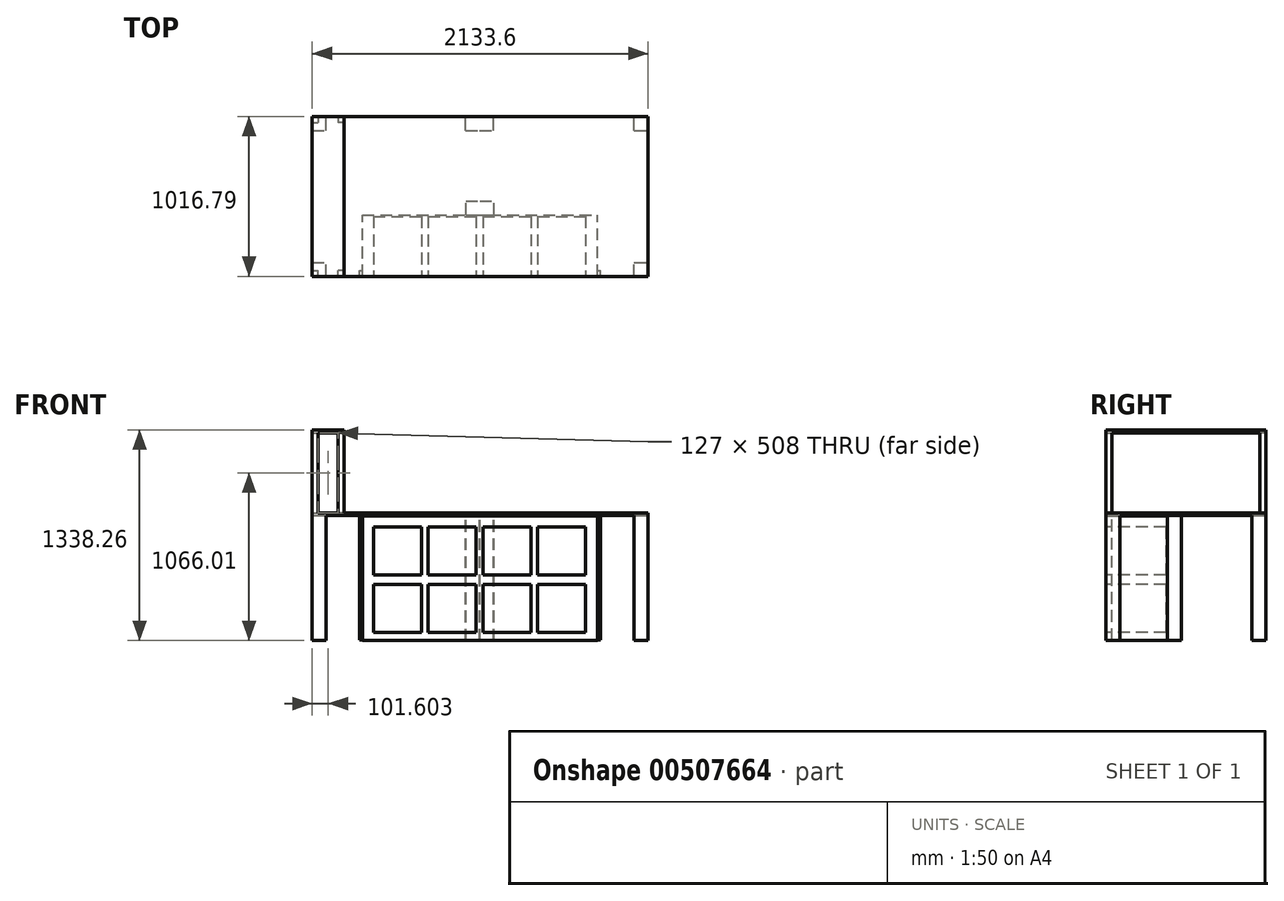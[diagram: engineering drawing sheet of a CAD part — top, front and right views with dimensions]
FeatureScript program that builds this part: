
annotation { "Feature Type Name" : "Feature", "Feature Type Description" : "" }
export const myFeature = defineFeature(function(context is Context, id is Id, definition is map)
    precondition{}
    {
        {
            var Q0;
            Q0=qCreatedBy(makeId("Top.planeOp"),FACE);
            var sketch = newSketch(context, id + "F0", { "sketchPlane" : qUnion([Q0])});
            skLineSegment(sketch, "E0", {"start": v(-1062.93, -24.93) * mm, "end": v(1070.67, -24.93) * mm});
            skLineSegment(sketch, "E1", {"start": v(-1062.93, -24.93) * mm, "end": v(-1062.93, -1040.93) * mm});
            skLineSegment(sketch, "E2", {"start": v(-1062.93, -1040.93) * mm, "end": v(1070.67, -1040.93) * mm});
            skLineSegment(sketch, "E3", {"start": v(1070.67, -1040.93) * mm, "end": v(1070.67, -24.93) * mm});
            skLineSegment(sketch, "E4", {"start": v(0, -1040.93) * mm, "end": v(0, -24.93) * mm});
            skSolve(sketch);
        }
        {
            var Q0;
            {var subQ0=sQuery(id+"F0.wireOp",EDGE,"E1");Q0=makeQuery(id+"F0.imprint","IMPRINT",FACE,{"disambiguationData":[TD([[makeQuery(id+"F0.imprint","IMPRINT",EDGE,{"derivedFrom":subQ0}),1.0]])]});}
            var Q1;
            {var subQ0=sQuery(id+"F0.wireOp",EDGE,"E3");Q1=makeQuery(id+"F0.imprint","IMPRINT",FACE,{"disambiguationData":[TD([[makeQuery(id+"F0.imprint","IMPRINT",EDGE,{"derivedFrom":subQ0}),1.0]])]});}
            extrude(context, id + "F1", {"entities" : qUnion([Q0, Q1]), "depth" : 18.26 * mm});
        }
        {
            var Q0;
            Q0=makeQuery(id+"F1.opExtrude","CAP_FACE",FACE,{"disambiguationData":[OSD([sQuery(id+"F0.wireOp",EDGE,"E0"),sQuery(id+"F0.wireOp",EDGE,"E1"),sQuery(id+"F0.wireOp",EDGE,"E2"),sQuery(id+"F0.wireOp",EDGE,"E3")])],"isStart":true});
            var sketch = newSketch(context, id + "F2", { "sketchPlane" : qUnion([Q0])});
            skLineSegment(sketch, "E5", {"start": v(3.87, 1040.93) * mm, "end": v(0, 24.93) * mm, "construction": true});
            skPoint(sketch, "E5.endSnap0", {"position": v(3.87, 24.93) * mm});
            skLineSegment(sketch, "E6.bottom", {"start": v(-743.74, 1040.93) * mm, "end": v(748.5, 1040.93) * mm});
            skLineSegment(sketch, "E6.top", {"start": v(-743.74, 650.4) * mm, "end": v(748.5, 650.4) * mm, "construction": true});
            skLineSegment(sketch, "E6.left", {"start": v(-743.74, 1040.93) * mm, "end": v(-743.74, 650.4) * mm, "construction": true});
            skLineSegment(sketch, "E6.right", {"start": v(748.5, 1040.93) * mm, "end": v(748.5, 650.4) * mm, "construction": true});
            skLineSegment(sketch, "E7", {"start": v(2.38, 650.4) * mm, "end": v(2.38, 1040.93) * mm, "construction": true});
            skLineSegment(sketch, "E8.bottom", {"start": v(-1062.93, 1040.93) * mm, "end": v(-974.03, 1040.93) * mm});
            skLineSegment(sketch, "E8.top", {"start": v(-1062.93, 952.03) * mm, "end": v(-974.03, 952.03) * mm});
            skLineSegment(sketch, "E8.left", {"start": v(-1062.93, 1040.93) * mm, "end": v(-1062.93, 952.03) * mm});
            skLineSegment(sketch, "E8.right", {"start": v(-974.03, 1040.93) * mm, "end": v(-974.03, 952.03) * mm});
            skLineSegment(sketch, "E9.bottom", {"start": v(-1062.93, 113.83) * mm, "end": v(-974.03, 113.83) * mm});
            skLineSegment(sketch, "E9.top", {"start": v(-1062.93, 24.93) * mm, "end": v(-974.03, 24.93) * mm});
            skLineSegment(sketch, "E9.left", {"start": v(-1062.93, 113.83) * mm, "end": v(-1062.93, 24.93) * mm});
            skLineSegment(sketch, "E9.right", {"start": v(-974.03, 113.83) * mm, "end": v(-974.03, 24.93) * mm});
            skLineSegment(sketch, "E10.bottom", {"start": v(981.77, 113.83) * mm, "end": v(1070.67, 113.83) * mm});
            skLineSegment(sketch, "E10.top", {"start": v(981.77, 24.93) * mm, "end": v(1070.67, 24.93) * mm});
            skLineSegment(sketch, "E10.left", {"start": v(981.77, 113.83) * mm, "end": v(981.77, 24.93) * mm});
            skLineSegment(sketch, "E10.right", {"start": v(1070.67, 113.83) * mm, "end": v(1070.67, 24.93) * mm});
            skLineSegment(sketch, "E11.bottom", {"start": v(981.77, 1040.93) * mm, "end": v(1070.67, 1040.93) * mm});
            skLineSegment(sketch, "E11.top", {"start": v(981.77, 952.03) * mm, "end": v(1070.67, 952.03) * mm});
            skLineSegment(sketch, "E11.left", {"start": v(981.77, 1040.93) * mm, "end": v(981.77, 952.03) * mm});
            skLineSegment(sketch, "E11.right", {"start": v(1070.67, 1040.93) * mm, "end": v(1070.67, 952.03) * mm});
            skLineSegment(sketch, "E12.bottom", {"start": v(-86.52, 650.4) * mm, "end": v(2.38, 650.4) * mm});
            skLineSegment(sketch, "E12.top", {"start": v(-86.86, 561.5) * mm, "end": v(2.05, 561.5) * mm});
            skLineSegment(sketch, "E12.left", {"start": v(-86.52, 650.4) * mm, "end": v(-86.86, 561.5) * mm});
            skLineSegment(sketch, "E12.right", {"start": v(2.38, 650.4) * mm, "end": v(2.05, 561.5) * mm});
            skLineSegment(sketch, "E13.bottom", {"start": v(-88.56, 113.83) * mm, "end": v(0.34, 113.83) * mm});
            skLineSegment(sketch, "E13.top", {"start": v(-88.9, 24.93) * mm, "end": v(0, 24.93) * mm});
            skLineSegment(sketch, "E13.left", {"start": v(-88.56, 113.83) * mm, "end": v(-88.9, 24.93) * mm});
            skLineSegment(sketch, "E13.right", {"start": v(0.34, 113.83) * mm, "end": v(0, 24.93) * mm});
            skLineSegment(sketch, "E14.bottom", {"start": v(2.38, 650.4) * mm, "end": v(91.28, 650.07) * mm});
            skLineSegment(sketch, "E14.top", {"start": v(2.05, 561.5) * mm, "end": v(90.94, 561.17) * mm});
            skLineSegment(sketch, "E14.right", {"start": v(91.28, 650.07) * mm, "end": v(90.94, 561.17) * mm});
            skLineSegment(sketch, "E15.bottom", {"start": v(0.34, 113.83) * mm, "end": v(89.24, 113.5) * mm});
            skLineSegment(sketch, "E15.top", {"start": v(0, 24.93) * mm, "end": v(88.9, 24.6) * mm});
            skLineSegment(sketch, "E15.right", {"start": v(89.24, 113.5) * mm, "end": v(88.9, 24.6) * mm});
            skSolve(sketch);
        }
        {
            var Q0;
            Q0 = qSketchRegion(id + "F2", true);
            extrude(context, id + "F3", {"entities" : qUnion([Q0]), "operationType" : NewBodyOperationType.ADD, "depth" : 793.75 * mm});
        }
        {
            var Q0;
            {var subQ6=sQuery(id+"F2.wireOp",EDGE,"E6.bottom");Q0=makeQuery(id+"F2.imprint","IMPRINT",FACE,{"disambiguationData":[TD([[makeQuery(id+"F2.imprint","IMPRINT",EDGE,{"derivedFrom":subQ6}),-1.0]])]});}
            cPlane(context, id + "F4", {"entities" : qUnion([Q0]), "cplaneType" : CPlaneType.OFFSET, "offset" : 3.17 * mm, "width" : 152.4 * mm, "height" : 152.4 * mm});
        }
        {
            var Q0;
            Q0=qCreatedBy(id+"F4.planeOp",FACE);
            var sketch = newSketch(context, id + "F5", { "sketchPlane" : qUnion([Q0])});
            skLineSegment(sketch, "E16", {"start": v(-744, 1041.4) * mm, "end": v(-744, 651.87) * mm});
            skLineSegment(sketch, "E17", {"start": v(-744, 651.87) * mm, "end": v(748.46, 651.87) * mm});
            skLineSegment(sketch, "E18", {"start": v(748.5, 1041.2) * mm, "end": v(748.46, 651.87) * mm});
            skLineSegment(sketch, "E19", {"start": v(-744, 1041.4) * mm, "end": v(748.5, 1041.2) * mm});
            skSolve(sketch);
        }
        {
            var Q0;
            Q0=makeQuery(id+"F5.imprint","IMPRINT",FACE,{"disambiguationData":[TD([[makeQuery(id+"F5.imprint","IMPRINT",EDGE,{"derivedFrom":sQuery(id+"F5.wireOp",EDGE,"E16")}),1.0]])]});
            extrude(context, id + "F6", {"entities" : qUnion([Q0]), "depth" : 790.57 * mm});
        }
        {
            var Q0;
            Q0=makeQuery(id+"F6.opExtrude","SWEPT_FACE",FACE,{"disambiguationData":[OSD([sQuery(id+"F5.wireOp",EDGE,"E19")])]});
            var sketch = newSketch(context, id + "F7", { "sketchPlane" : qUnion([Q0])});
            skLineSegment(sketch, "E20.bottom", {"start": v(-674.52, -72.87) * mm, "end": v(-369.72, -72.87) * mm});
            skLineSegment(sketch, "E20.top", {"start": v(-674.52, -377.67) * mm, "end": v(-369.72, -377.67) * mm});
            skLineSegment(sketch, "E20.left", {"start": v(-674.52, -72.87) * mm, "end": v(-674.52, -377.67) * mm});
            skLineSegment(sketch, "E20.right", {"start": v(-369.72, -72.87) * mm, "end": v(-369.72, -377.67) * mm});
            skLineSegment(sketch, "E21.0.1.0", {"start": v(-369.72, -436.09) * mm, "end": v(-369.72, -740.89) * mm});
            skLineSegment(sketch, "E21.0.1.1", {"start": v(-674.52, -436.09) * mm, "end": v(-674.52, -740.89) * mm});
            skLineSegment(sketch, "E21.0.1.2", {"start": v(-674.52, -740.89) * mm, "end": v(-369.72, -740.89) * mm});
            skLineSegment(sketch, "E21.0.1.3", {"start": v(-674.52, -436.09) * mm, "end": v(-369.72, -436.09) * mm});
            skLineSegment(sketch, "E21.1.0.0", {"start": v(-21.74, -72.87) * mm, "end": v(-21.74, -377.67) * mm});
            skLineSegment(sketch, "E21.1.0.1", {"start": v(-326.54, -72.87) * mm, "end": v(-326.54, -377.67) * mm});
            skLineSegment(sketch, "E21.1.0.2", {"start": v(-326.54, -377.67) * mm, "end": v(-21.74, -377.67) * mm});
            skLineSegment(sketch, "E21.1.0.3", {"start": v(-326.54, -72.87) * mm, "end": v(-21.74, -72.87) * mm});
            skLineSegment(sketch, "E21.1.1.0", {"start": v(-21.74, -436.09) * mm, "end": v(-21.74, -740.89) * mm});
            skLineSegment(sketch, "E21.1.1.1", {"start": v(-326.54, -436.09) * mm, "end": v(-326.54, -740.89) * mm});
            skLineSegment(sketch, "E21.1.1.2", {"start": v(-326.54, -740.89) * mm, "end": v(-21.74, -740.89) * mm});
            skLineSegment(sketch, "E21.1.1.3", {"start": v(-326.54, -436.09) * mm, "end": v(-21.74, -436.09) * mm});
            skLineSegment(sketch, "E21.2.0.0", {"start": v(326.24, -72.87) * mm, "end": v(326.24, -377.67) * mm});
            skLineSegment(sketch, "E21.2.0.1", {"start": v(21.44, -72.87) * mm, "end": v(21.44, -377.67) * mm});
            skLineSegment(sketch, "E21.2.0.2", {"start": v(21.44, -377.67) * mm, "end": v(326.24, -377.67) * mm});
            skLineSegment(sketch, "E21.2.0.3", {"start": v(21.44, -72.87) * mm, "end": v(326.24, -72.87) * mm});
            skLineSegment(sketch, "E21.2.1.0", {"start": v(326.24, -436.09) * mm, "end": v(326.24, -740.89) * mm});
            skLineSegment(sketch, "E21.2.1.1", {"start": v(21.44, -436.09) * mm, "end": v(21.44, -740.89) * mm});
            skLineSegment(sketch, "E21.2.1.2", {"start": v(21.44, -740.89) * mm, "end": v(326.24, -740.89) * mm});
            skLineSegment(sketch, "E21.2.1.3", {"start": v(21.44, -436.09) * mm, "end": v(326.24, -436.09) * mm});
            skLineSegment(sketch, "E21.3.0.0", {"start": v(674.22, -72.87) * mm, "end": v(674.22, -377.67) * mm});
            skLineSegment(sketch, "E21.3.0.1", {"start": v(369.42, -72.87) * mm, "end": v(369.42, -377.67) * mm});
            skLineSegment(sketch, "E21.3.0.2", {"start": v(369.42, -377.67) * mm, "end": v(674.22, -377.67) * mm});
            skLineSegment(sketch, "E21.3.0.3", {"start": v(369.42, -72.87) * mm, "end": v(674.22, -72.87) * mm});
            skLineSegment(sketch, "E21.3.1.0", {"start": v(674.22, -436.09) * mm, "end": v(674.22, -740.89) * mm});
            skLineSegment(sketch, "E21.3.1.1", {"start": v(369.42, -436.09) * mm, "end": v(369.42, -740.89) * mm});
            skLineSegment(sketch, "E21.3.1.2", {"start": v(369.42, -740.89) * mm, "end": v(674.22, -740.89) * mm});
            skLineSegment(sketch, "E21.3.1.3", {"start": v(369.42, -436.09) * mm, "end": v(674.22, -436.09) * mm});
            skLineSegment(sketch, "E21.direction1", {"start": v(-674.52, -377.67) * mm, "end": v(-326.54, -377.67) * mm, "construction": true});
            skLineSegment(sketch, "E21.direction2", {"start": v(-674.52, -377.67) * mm, "end": v(-674.52, -740.89) * mm, "construction": true});
            skSolve(sketch);
        }
        {
            var Q0;
            Q0 = qSketchRegion(id + "F7", true);
            extrude(context, id + "F8", {"entities" : qUnion([Q0]), "operationType" : NewBodyOperationType.REMOVE, "oppositeDirection" : true, "depth" : 381 * mm});
        }
        {
            var Q0;
            {var subQ6=sQuery(id+"F2.wireOp",EDGE,"E6.bottom");Q0=makeQuery(id+"F2.imprint","IMPRINT",FACE,{"disambiguationData":[TD([[makeQuery(id+"F2.imprint","IMPRINT",EDGE,{"derivedFrom":subQ6}),-1.0]])]});}
            var sketch = newSketch(context, id + "F9", { "sketchPlane" : qUnion([Q0])});
            skLineSegment(sketch, "E22.bottom", {"start": v(748.8, 1040.9) * mm, "end": v(767.86, 1040.9) * mm});
            skLineSegment(sketch, "E22.top", {"start": v(748.8, 1002.8) * mm, "end": v(767.86, 1002.8) * mm});
            skLineSegment(sketch, "E22.left", {"start": v(748.8, 1040.9) * mm, "end": v(748.8, 1002.8) * mm});
            skLineSegment(sketch, "E22.right", {"start": v(767.86, 1040.9) * mm, "end": v(767.86, 1002.8) * mm});
            skLineSegment(sketch, "E23.bottom", {"start": v(-763.16, 1040.9) * mm, "end": v(-744.11, 1040.9) * mm});
            skLineSegment(sketch, "E23.top", {"start": v(-763.16, 1002.8) * mm, "end": v(-744.11, 1002.8) * mm});
            skLineSegment(sketch, "E23.left", {"start": v(-763.16, 1040.9) * mm, "end": v(-763.16, 1002.8) * mm});
            skLineSegment(sketch, "E23.right", {"start": v(-744.11, 1040.9) * mm, "end": v(-744.11, 1002.8) * mm});
            skSolve(sketch);
        }
        {
            var Q0;
            Q0 = qSketchRegion(id + "F9", true);
            extrude(context, id + "F10", {"entities" : qUnion([Q0]), "operationType" : NewBodyOperationType.ADD, "depth" : 790.57 * mm});
        }
        {
            var Q0;
            Q0=makeQuery(id+"F1.opExtrude","CAP_FACE",FACE,{"disambiguationData":[OSD([sQuery(id+"F0.wireOp",EDGE,"E0"),sQuery(id+"F0.wireOp",EDGE,"E1"),sQuery(id+"F0.wireOp",EDGE,"E2"),sQuery(id+"F0.wireOp",EDGE,"E3")])],"isStart":false});
            var sketch = newSketch(context, id + "F11", { "sketchPlane" : qUnion([Q0])});
            skLineSegment(sketch, "E24.bottom", {"start": v(-1062.93, -24.93) * mm, "end": v(-859.73, -24.93) * mm, "construction": true});
            skLineSegment(sketch, "E24.top", {"start": v(-1062.93, -1040.93) * mm, "end": v(-859.73, -1040.93) * mm, "construction": true});
            skLineSegment(sketch, "E24.left", {"start": v(-1062.93, -24.93) * mm, "end": v(-1062.93, -1040.93) * mm, "construction": true});
            skLineSegment(sketch, "E24.right", {"start": v(-859.73, -24.93) * mm, "end": v(-859.73, -1040.93) * mm, "construction": true});
            skLineSegment(sketch, "E25.bottom", {"start": v(-1062.93, -24.93) * mm, "end": v(-1024.83, -24.93) * mm});
            skLineSegment(sketch, "E25.top", {"start": v(-1062.93, -63.03) * mm, "end": v(-1024.83, -63.03) * mm});
            skLineSegment(sketch, "E25.left", {"start": v(-1062.93, -24.93) * mm, "end": v(-1062.93, -63.03) * mm});
            skLineSegment(sketch, "E25.right", {"start": v(-1024.83, -24.93) * mm, "end": v(-1024.83, -63.03) * mm});
            skLineSegment(sketch, "E26.bottom", {"start": v(-859.73, -24.93) * mm, "end": v(-897.83, -24.93) * mm});
            skLineSegment(sketch, "E26.top", {"start": v(-859.73, -63.03) * mm, "end": v(-897.83, -63.03) * mm});
            skLineSegment(sketch, "E26.left", {"start": v(-859.73, -24.93) * mm, "end": v(-859.73, -63.03) * mm});
            skLineSegment(sketch, "E26.right", {"start": v(-897.83, -24.93) * mm, "end": v(-897.83, -63.03) * mm});
            skLineSegment(sketch, "E27.bottom", {"start": v(-1062.93, -1040.93) * mm, "end": v(-1024.83, -1040.93) * mm});
            skLineSegment(sketch, "E27.top", {"start": v(-1062.93, -1002.83) * mm, "end": v(-1024.83, -1002.83) * mm});
            skLineSegment(sketch, "E27.left", {"start": v(-1062.93, -1040.93) * mm, "end": v(-1062.93, -1002.83) * mm});
            skLineSegment(sketch, "E27.right", {"start": v(-1024.83, -1040.93) * mm, "end": v(-1024.83, -1002.83) * mm});
            skLineSegment(sketch, "E28.bottom", {"start": v(-859.73, -1040.93) * mm, "end": v(-897.83, -1040.93) * mm});
            skLineSegment(sketch, "E28.top", {"start": v(-859.73, -1002.83) * mm, "end": v(-897.83, -1002.83) * mm});
            skLineSegment(sketch, "E28.left", {"start": v(-859.73, -1040.93) * mm, "end": v(-859.73, -1002.83) * mm});
            skLineSegment(sketch, "E28.right", {"start": v(-897.83, -1040.93) * mm, "end": v(-897.83, -1002.83) * mm});
            skSolve(sketch);
        }
        {
            var Q0;
            Q0 = qSketchRegion(id + "F11", true);
            extrude(context, id + "F12", {"entities" : qUnion([Q0]), "operationType" : NewBodyOperationType.ADD, "depth" : 508 * mm});
        }
        {
            var Q0;
            Q0=makeQuery(id+"F12.opExtrude","CAP_FACE",FACE,{"disambiguationData":[OSD([sQuery(id+"F11.wireOp",EDGE,"E27.bottom"),sQuery(id+"F11.wireOp",EDGE,"E27.top"),sQuery(id+"F11.wireOp",EDGE,"E27.left"),sQuery(id+"F11.wireOp",EDGE,"E27.right")])],"isStart":false});
            var sketch = newSketch(context, id + "F13", { "sketchPlane" : qUnion([Q0])});
            skLineSegment(sketch, "E29.bottom", {"start": v(-1062.93, -1040.93) * mm, "end": v(-859.73, -1040.93) * mm});
            skLineSegment(sketch, "E29.top", {"start": v(-1062.93, -24.93) * mm, "end": v(-859.73, -24.93) * mm});
            skLineSegment(sketch, "E29.left", {"start": v(-1062.93, -1040.93) * mm, "end": v(-1062.93, -24.93) * mm});
            skLineSegment(sketch, "E29.right", {"start": v(-859.73, -1040.93) * mm, "end": v(-859.73, -24.93) * mm});
            skSolve(sketch);
        }
        {
            var Q0;
            Q0 = qSketchRegion(id + "F13", true);
            extrude(context, id + "F14", {"entities" : qUnion([Q0]), "operationType" : NewBodyOperationType.ADD, "depth" : 18.26 * mm});
        }
    });
